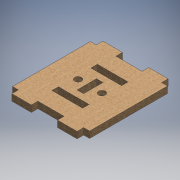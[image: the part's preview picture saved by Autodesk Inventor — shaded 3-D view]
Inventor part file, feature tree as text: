
AUTODESK INVENTOR PART (.ipt)
format: ipt  version: 2016 (Build 200138000, 138)  size: 177,664 bytes
history: native  units: mm
features: extrude x1, sketch x1
ambient origin geometry x8: Origin, YZ Plane, XZ Plane, XY Plane, X Axis, Y Axis, Z Axis, Center Point
bodies: Body1 (feature_tree)
feature tree (2):
  extrude  "Extrusion4"  Depth=75.835317mm
  sketch  "Sketch1"  dims[d0=75.0mm d1=75.835317mm d2=18.958829mm d3=6.39mm d4=12.78mm d21=6.39mm d22=29.89mm d24=18.958829mm d25=6.39mm d30=37.917659mm d41=6.6675mm d42=6.39mm d43=0.0mm]
